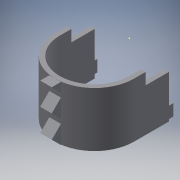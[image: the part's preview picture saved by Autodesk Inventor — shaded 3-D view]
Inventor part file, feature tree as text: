
AUTODESK INVENTOR PART (.ipt)
format: ipt  version: 2016 (Build 200138000, 138)  size: 245,760 bytes
history: native  units: in
note: dims shown in document units (in); Inventor stores cm internally (conversion verified against a paired STEP export)
features: sketch x12, extrude x11, reference x10, projected_geometry x2, plane x1
ambient origin geometry x8: Origin, YZ Plane, XZ Plane, XY Plane, X Axis, Y Axis, Z Axis, Center Point
bodies: Solid1 (feature_tree)
feature tree (36):
  extrude  "Extrusion1"  Depth=1.5in TaperAngle=0.0deg
  extrude  "Extrusion2"  Depth=0.1969in TaperAngle=0.0deg
  extrude  "Extrusion3"  [1 undecoded]
  extrude  "Extrusion4"  Depth=0.3937in
  plane  "Work Plane1"
  sketch  "Sketch5"  dims[d12=1.9685in d14=0.9774in d15=0.3937in d17=1.0in d19=0.5in d20=0.0in]
  extrude  "Extrusion5"  Depth=0.5in TaperAngle=0.0deg
  extrude  "Extrusion6"  Depth=0.197in TaperAngle=0.0deg
  extrude  "Extrusion7"  Depth=16.0in TaperAngle=0.0deg
  extrude  "Extrusion8"  Depth=0.5in TaperAngle=0.0deg
  extrude  "Extrusion9"  [1 undecoded]
  extrude  "Extrusion10"  [1 undecoded]
  extrude  "Extrusion11"  [1 undecoded]
  sketch  "Sketch1"  dims[d0=0.1969in d1=1.5in d2=0.0in]
  reference  "Reference1"
  sketch  "Sketch2"  dims[d3=4.6969in d4=0.0in d5=0.1969in d6=0.0in]
  sketch  "Sketch3"  dims[d7=0.1969in d8=0.0in d9=-1.697in]
  sketch  "Sketch4"  dims[d10=0.7874in d11=0.3937in]
  reference  "Reference2"
  sketch  "Sketch6"  dims[d21=0.197in d22=0.0in d23=2.0in d24=0.0in]
  sketch  "Sketch8"  dims[d25=2.0in d26=0.0in d27=16.0in d28=0.0in]
  reference  "Reference3"
  reference  "Reference5"
  reference  "Reference6"
  reference  "Reference7"
  reference  "Reference8"
  reference  "Reference9"
  sketch  "Sketch9"  dims[d29=0.5in d30=6575.0in d31=0.0in]
  reference  "Reference10"
  sketch  "Sketch10"  dims[d32=0.5in d33=0.0in]
  reference  "Reference11"
  sketch  "Sketch11"
  sketch  "Sketch12"
  sketch  "Sketch13"
  projected_geometry  "Projected Loop1"
  projected_geometry  "Projected Loop2"
note: 4 required parameter values undecoded (feature->parameter linkage not recoverable at this tier; creation-order binding heuristic only, values carry confidence <= 0.55)
